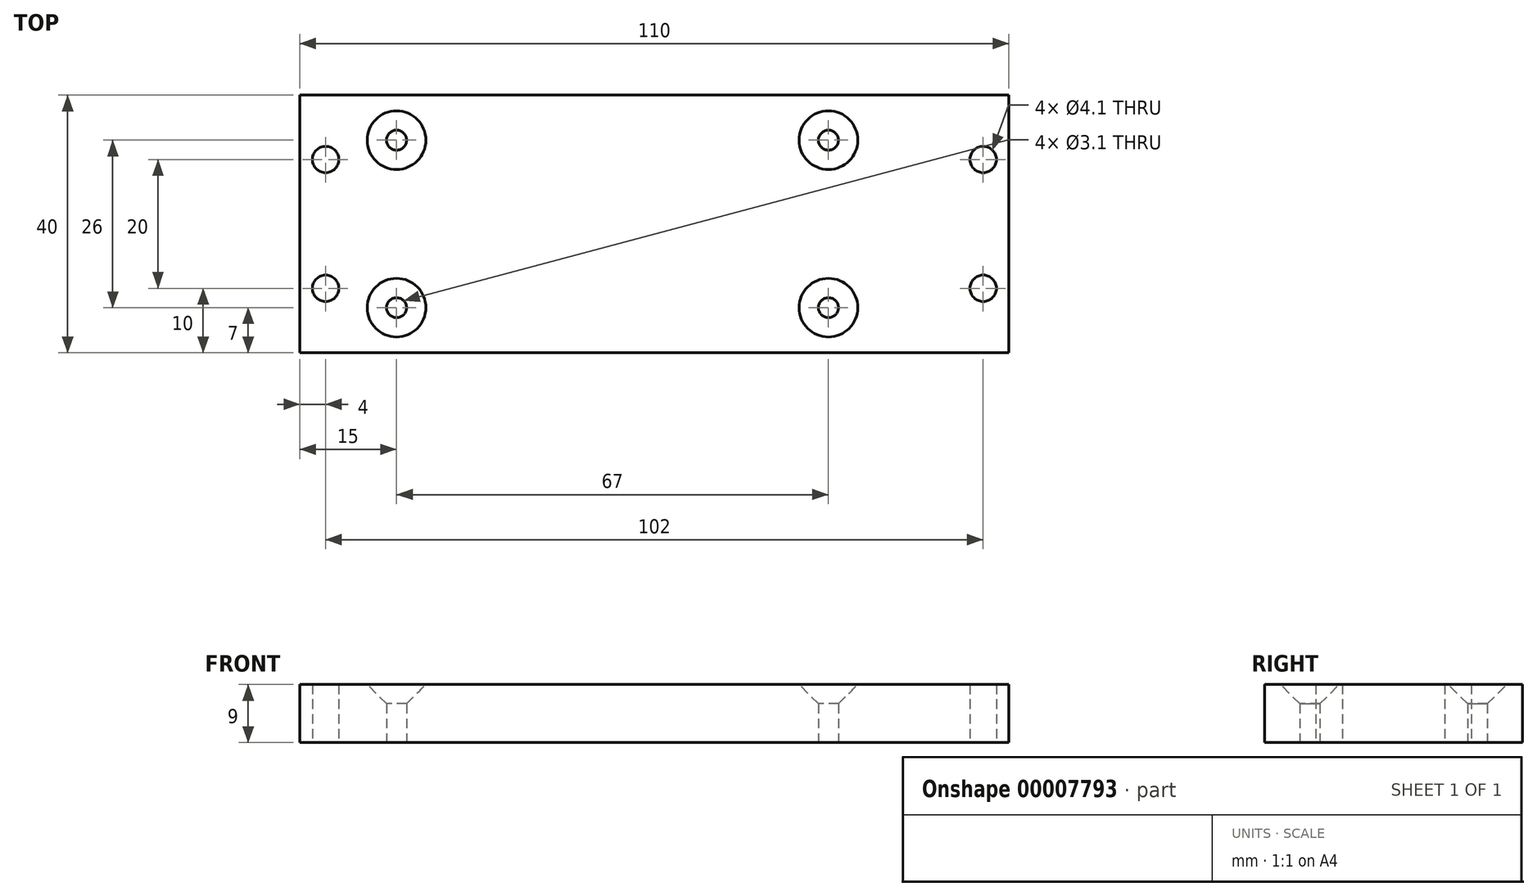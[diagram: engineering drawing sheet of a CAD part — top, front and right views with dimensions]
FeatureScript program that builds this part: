
annotation { "Feature Type Name" : "Feature", "Feature Type Description" : "" }
export const myFeature = defineFeature(function(context is Context, id is Id, definition is map)
    precondition{}
    {
        {
            var Q0;
            Q0=qCreatedBy(makeId("Top.planeOp"),FACE);
            var sketch = newSketch(context, id + "F0", { "sketchPlane" : qUnion([Q0])});
            skLineSegment(sketch, "E0.rect.bottom", {"start": v(55, -20) * mm, "end": v(-55, -20) * mm});
            skLineSegment(sketch, "E0.rect.top", {"start": v(55, 20) * mm, "end": v(-55, 20) * mm});
            skLineSegment(sketch, "E0.rect.left", {"start": v(55, -20) * mm, "end": v(55, 20) * mm});
            skLineSegment(sketch, "E0.rect.right", {"start": v(-55, -20) * mm, "end": v(-55, 20) * mm});
            skPoint(sketch, "E0.rect.middle", {"position": v(0, 0) * mm});
            skLineSegment(sketch, "E1", {"start": v(-53.6, 0) * mm, "end": v(57.16, 0) * mm});
            skCircle(sketch, "E2", {"center": v(-51, 10) * mm, "radius": 2.05 * mm});
            skLineSegment(sketch, "E3", {"start": v(0, 22.8) * mm, "end": v(0, -23.19) * mm});
            skCircle(sketch, "E4.0.MirrorC", {"center": v(-51, -10) * mm, "radius": 2.05 * mm});
            skCircle(sketch, "E5.0.MirrorC", {"center": v(51, 10) * mm, "radius": 2.05 * mm});
            skCircle(sketch, "E6.0.MirrorC", {"center": v(51, -10) * mm, "radius": 2.05 * mm});
            skCircle(sketch, "E7", {"center": v(-40, 13) * mm, "radius": 1.55 * mm});
            skCircle(sketch, "E8", {"center": v(27, 13) * mm, "radius": 1.55 * mm});
            skCircle(sketch, "E9.0.MirrorC", {"center": v(-40, -13) * mm, "radius": 1.55 * mm});
            skCircle(sketch, "E10.0.MirrorC", {"center": v(27, -13) * mm, "radius": 1.55 * mm});
            skSolve(sketch);
        }
        {
            var Q0;
            {var subQ3=sQuery(id+"F0.wireOp",EDGE,"E0.rect.bottom");var subQ5=sQuery(id+"F0.wireOp",EDGE,"E0.rect.right");var subQ7=makeQuery(id+"F0.imprint","INTERSECT",VERTEX,{"derivedFrom":[subQ3,subQ5]});Q0=makeQuery(id+"F0.imprint","IMPRINT",FACE,{"disambiguationData":[TD([[makeQuery(id+"F0.imprint","IMPRINT",EDGE,{"disambiguationData":[TD([[subQ7,1.0]])],"derivedFrom":subQ3}),-1.0]])]});}
            var Q1;
            Q1=makeQuery(id+"F0.imprint","IMPRINT",FACE,{"disambiguationData":[TD([[makeQuery(id+"F0.imprint","IMPRINT",EDGE,{"derivedFrom":sQuery(id+"F0.wireOp",EDGE,"E2")}),-1.0]])]});
            var Q2;
            {var subQ3=sQuery(id+"F0.wireOp",EDGE,"E0.rect.top");var subQ5=sQuery(id+"F0.wireOp",EDGE,"E0.rect.left");var subQ7=makeQuery(id+"F0.imprint","INTERSECT",VERTEX,{"derivedFrom":[subQ3,subQ5]});Q2=makeQuery(id+"F0.imprint","IMPRINT",FACE,{"disambiguationData":[TD([[makeQuery(id+"F0.imprint","IMPRINT",EDGE,{"disambiguationData":[TD([[subQ7,-1.0]])],"derivedFrom":subQ3}),1.0]])]});}
            var Q3;
            {var subQ3=sQuery(id+"F0.wireOp",EDGE,"E0.rect.bottom");var subQ5=sQuery(id+"F0.wireOp",EDGE,"E0.rect.left");var subQ7=makeQuery(id+"F0.imprint","INTERSECT",VERTEX,{"derivedFrom":[subQ3,subQ5]});Q3=makeQuery(id+"F0.imprint","IMPRINT",FACE,{"disambiguationData":[TD([[makeQuery(id+"F0.imprint","IMPRINT",EDGE,{"disambiguationData":[TD([[subQ7,-1.0]])],"derivedFrom":subQ3}),-1.0]])]});}
            extrude(context, id + "F1", {"entities" : qUnion([Q0, Q1, Q2, Q3]), "depth" : 9 * mm});
        }
        {
            var Q0;
            Q0=makeQuery(id+"F1.opExtrude","CAP_EDGE",EDGE,{"disambiguationData":[OSD([sQuery(id+"F0.wireOp",EDGE,"E9.0.MirrorC")])],"isStart":false});
            var Q1;
            Q1=makeQuery(id+"F1.opExtrude","CAP_EDGE",EDGE,{"disambiguationData":[OSD([sQuery(id+"F0.wireOp",EDGE,"E7")])],"isStart":false});
            var Q2;
            Q2=makeQuery(id+"F1.opExtrude","CAP_EDGE",EDGE,{"disambiguationData":[OSD([sQuery(id+"F0.wireOp",EDGE,"E8")])],"isStart":false});
            var Q3;
            Q3=makeQuery(id+"F1.opExtrude","CAP_EDGE",EDGE,{"disambiguationData":[OSD([sQuery(id+"F0.wireOp",EDGE,"E10.0.MirrorC")])],"isStart":false});
            chamfer(context, id + "F2", {"entities" : qUnion([Q0, Q1, Q2, Q3]), "width" : 3 * mm, "tangentPropagation" : true});
        }
    });
